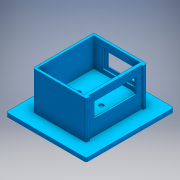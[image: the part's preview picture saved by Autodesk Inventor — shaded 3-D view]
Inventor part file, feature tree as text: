
AUTODESK INVENTOR PART (.ipt)
format: ipt  version: 2016 (Build 200138000, 138)  size: 253,440 bytes
history: native  units: mm
features: extrude x10, sketch x10
ambient origin geometry x8: Origin, YZ Plane, XZ Plane, XY Plane, X Axis, Y Axis, Z Axis, Center Point
bodies: Solid1 (feature_tree)
feature tree (20):
  extrude  "chamberBase"  Depth=85.0mm
  extrude  "chamberWallExt"  Depth=42.5mm
  extrude  "chamberIntExt"  Depth=10.0mm
  extrude  "rectCoverSlipMountExt"  Depth=10.0mm
  extrude  "rectCoverSlipWindow"  Depth=2.0mm
  extrude  "illObjExt"  Depth=70.0mm
  extrude  "viewingWindCoverSlipMount"  Depth=40.0mm
  extrude  "viewingWindExt"  Depth=2.0mm
  extrude  "sampleHolderMagnets"  Depth=3.0mm
  extrude  "xyStageMount"  Depth=37.5mm TaperAngle=0.0deg
  sketch  "Sketch1"  dims[d0=85.0mm d1=95.0mm]
  sketch  "Sketch2"  dims[d2=47.5mm d3=42.5mm]
  sketch  "Sketch3"  dims[d4=2.0mm d5=10.0mm]
  sketch  "Sketch4"  dims[d6=10.0mm d7=10.0mm]
  sketch  "Sketch5"  dims[d8=10.0mm d9=2.0mm]
  sketch  "Sketch7"  dims[d10=5.0mm d11=0.0mm d12=70.0mm]
  sketch  "Sketch8"  dims[d13=80.0mm d14=40.0mm]
  sketch  "Sketch9"  dims[d15=35.0mm d16=2.0mm]
  sketch  "Sketch10"  dims[d17=50.0mm d18=0.0mm d19=3.0mm]
  sketch  "Sketch13"  dims[d21=3.0mm d23=37.5mm d24=0.0mm d25=65.0mm d26=30.0mm d27=32.5mm d28=45.0mm d29=2.0mm d30=0.0mm d31=55.0mm d32=20.0mm d33=27.5mm d34=40.0mm d35=2.0mm d36=0.0mm d42=70.0mm d43=35.0mm d44=2.0mm d45=0.0mm d46=3.0mm d47=6.0mm d48=25.0mm d49=45.0mm d52=42.5mm d53=2.0mm d54=0.0mm d55=35.0mm d56=17.0mm d58=38.5mm d59=2.0mm d60=0.0mm d70=5.65mm d71=5.65mm d72=5.65mm d73=5.65mm d74=5.65mm d75=15.0mm d76=15.0mm d77=15.0mm d78=15.0mm d79=2.0mm d80=0.0mm d98=2.65mm d99=2.65mm d100=2.65mm d101=2.65mm d102=2.65mm d103=55.0mm d104=55.0mm d105=50.0mm d106=50.0mm d107=2.0mm d108=0.0mm d109=4.5mm d110=5.0mm]
